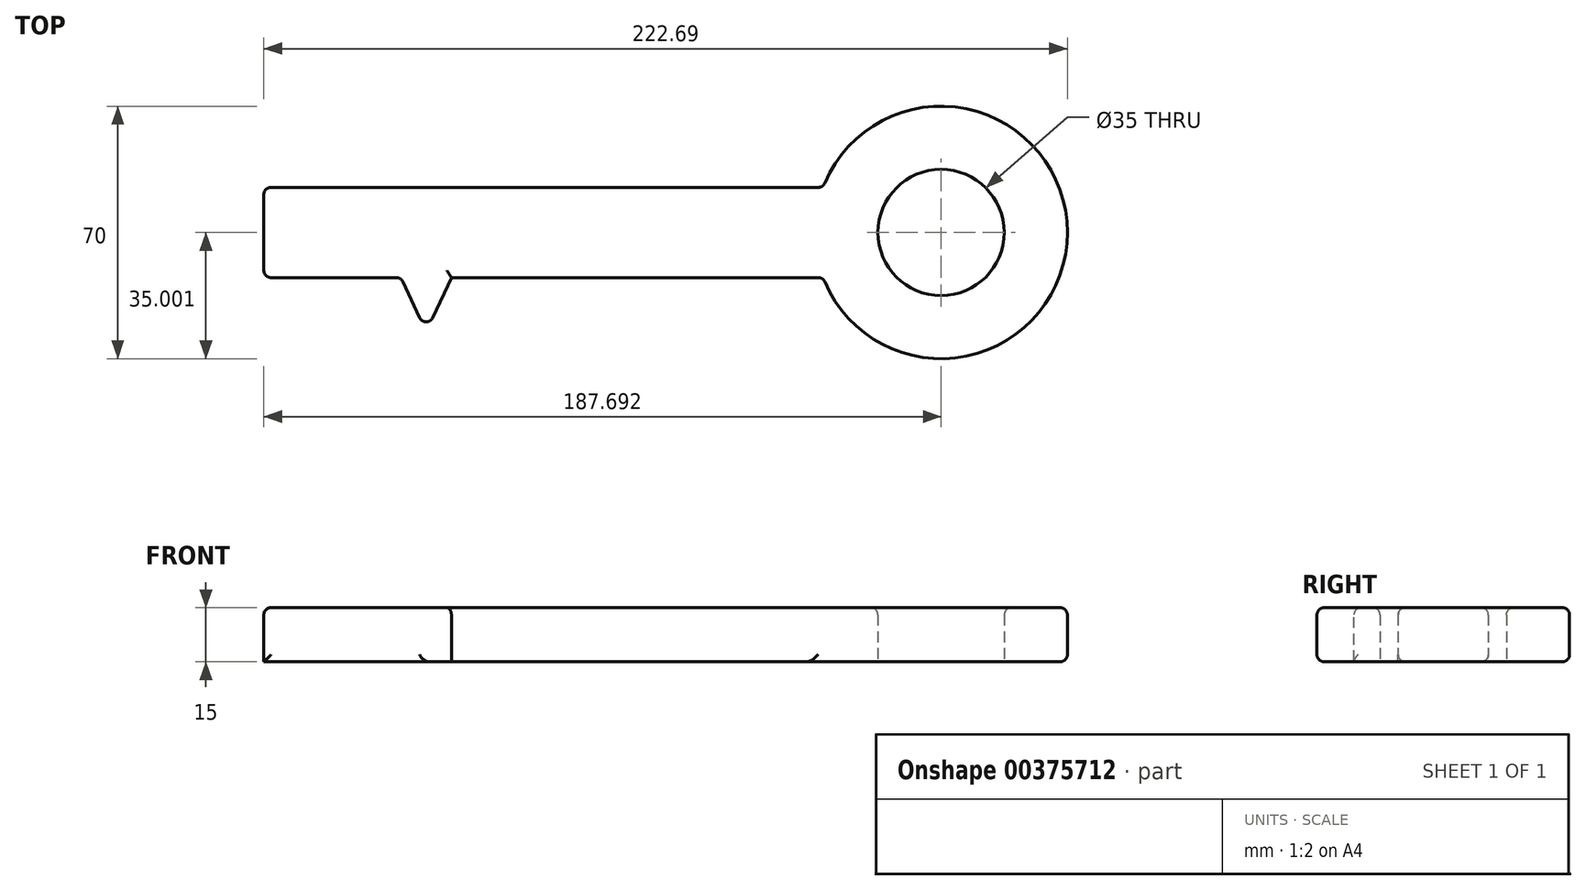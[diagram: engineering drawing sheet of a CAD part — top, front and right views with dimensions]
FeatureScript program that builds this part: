
annotation { "Feature Type Name" : "Feature", "Feature Type Description" : "" }
export const myFeature = defineFeature(function(context is Context, id is Id, definition is map)
    precondition{}
    {
        {
            var Q0;
            Q0=qCreatedBy(makeId("Top.planeOp"),FACE);
            var sketch = newSketch(context, id + "F0", { "sketchPlane" : qUnion([Q0])});
            skLineSegment(sketch, "E0.bottom", {"start": v(-155, 9.98) * mm, "end": v(0, 9.98) * mm});
            skLineSegment(sketch, "E0.top", {"start": v(-155, -15.02) * mm, "end": v(0, -15.02) * mm});
            skLineSegment(sketch, "E0.left", {"start": v(-155, 9.98) * mm, "end": v(-155, -15.02) * mm});
            skLineSegment(sketch, "E0.right", {"start": v(0, 9.98) * mm, "end": v(0, -15.02) * mm});
            skLineSegment(sketch, "E1.bottom", {"start": v(-155, -15.02) * mm, "end": v(-145, -15.02) * mm});
            skLineSegment(sketch, "E1.top", {"start": v(-155, -45.02) * mm, "end": v(-145, -45.02) * mm});
            skLineSegment(sketch, "E1.left", {"start": v(-155, -15.02) * mm, "end": v(-155, -45.02) * mm});
            skLineSegment(sketch, "E1.right", {"start": v(-145, -15.02) * mm, "end": v(-145, -45.02) * mm});
            skLineSegment(sketch, "E2.bottom", {"start": v(-135, -15.02) * mm, "end": v(-127, -15.02) * mm});
            skLineSegment(sketch, "E2.top", {"start": v(-135, -30.02) * mm, "end": v(-127, -30.02) * mm});
            skLineSegment(sketch, "E2.left", {"start": v(-135, -15.02) * mm, "end": v(-135, -30.02) * mm});
            skLineSegment(sketch, "E2.right", {"start": v(-127, -15.02) * mm, "end": v(-127, -30.02) * mm});
            skLineSegment(sketch, "E3", {"start": v(-117, -15.02) * mm, "end": v(-110, -30.02) * mm});
            skLineSegment(sketch, "E4", {"start": v(-103, -15.02) * mm, "end": v(-110, -30.02) * mm});
            skArc(sketch, "E5", {"start": v(0, -15.02) * mm, "mid": v(67.7, -2.52) * mm, "end": v(0, 9.98) * mm});
            skCircle(sketch, "E6", {"center": v(32.7, -2.52) * mm, "radius": 17.5 * mm});
            skSolve(sketch);
        }
        {
            var Q0;
            Q0=makeQuery(id+"F0.imprint","IMPRINT",FACE,{"disambiguationData":[TD([[makeQuery(id+"F0.imprint","IMPRINT",EDGE,{"derivedFrom":sQuery(id+"F0.wireOp",EDGE,"E0.bottom")}),-1.0]])]});
            var Q1;
            Q1=makeQuery(id+"F0.imprint","IMPRINT",FACE,{"disambiguationData":[TD([[makeQuery(id+"F0.imprint","IMPRINT",EDGE,{"derivedFrom":sQuery(id+"F0.wireOp",EDGE,"E1.bottom")}),-1.0]])]});
            var Q2;
            Q2=makeQuery(id+"F0.imprint","IMPRINT",FACE,{"disambiguationData":[TD([[makeQuery(id+"F0.imprint","IMPRINT",EDGE,{"derivedFrom":sQuery(id+"F0.wireOp",EDGE,"E2.bottom")}),-1.0]])]});
            var Q3;
            {var subQ0=sQuery(id+"F0.wireOp",EDGE,"E3");Q3=makeQuery(id+"F0.imprint","IMPRINT",FACE,{"disambiguationData":[TD([[makeQuery(id+"F0.imprint","IMPRINT",EDGE,{"derivedFrom":subQ0}),1.0]])]});}
            var Q4;
            Q4=makeQuery(id+"F0.imprint","IMPRINT",FACE,{"disambiguationData":[TD([[makeQuery(id+"F0.imprint","IMPRINT",EDGE,{"derivedFrom":sQuery(id+"F0.wireOp",EDGE,"E0.right")}),1.0]])]});
            extrude(context, id + "F1", {"entities" : qUnion([Q0, Q1, Q2, Q3, Q4]), "depth" : 15 * mm});
        }
        {
            var Q0;
            Q0=makeQuery(id+"F1.opExtrude","CAP_EDGE",EDGE,{"disambiguationData":[OSD([sQuery(id+"F0.wireOp",EDGE,"E0.bottom")])],"isStart":false});
            var Q1;
            Q1=makeQuery(id+"F1.opExtrude","CAP_EDGE",EDGE,{"disambiguationData":[OSD([sQuery(id+"F0.wireOp",EDGE,"E0.left"),sQuery(id+"F0.wireOp",EDGE,"E1.left")])],"isStart":false});
            var Q2;
            Q2=makeQuery(id+"F1.opExtrude","CAP_EDGE",EDGE,{"disambiguationData":[OSD([sQuery(id+"F0.wireOp",EDGE,"E1.right")])],"isStart":false});
            var Q3;
            {var subQ0=sQuery(id+"F0.wireOp",EDGE,"E0.top");Q3=makeQuery(id+"F1.opExtrude","CAP_EDGE",EDGE,{"disambiguationData":[OSD([subQ0]),TDD([makeQuery(id+"F0.imprint","IMPRINT",EDGE,{"disambiguationData":[TD([[makeQuery(id+"F0.imprint","INTERSECT",VERTEX,{"derivedFrom":[subQ0,sQuery(id+"F0.wireOp",EDGE,"E1.bottom"),sQuery(id+"F0.wireOp",EDGE,"E1.right")]}),-1.0]])],"derivedFrom":subQ0})])],"isStart":false});}
            var Q4;
            Q4=makeQuery(id+"F1.opExtrude","CAP_EDGE",EDGE,{"disambiguationData":[OSD([sQuery(id+"F0.wireOp",EDGE,"E2.left")])],"isStart":false});
            var Q5;
            Q5=makeQuery(id+"F1.opExtrude","CAP_EDGE",EDGE,{"disambiguationData":[OSD([sQuery(id+"F0.wireOp",EDGE,"E2.right")])],"isStart":false});
            var Q6;
            Q6=makeQuery(id+"F1.opExtrude","CAP_EDGE",EDGE,{"disambiguationData":[OSD([sQuery(id+"F0.wireOp",EDGE,"E2.top")])],"isStart":false});
            var Q7;
            Q7=makeQuery(id+"F1.opExtrude","CAP_EDGE",EDGE,{"disambiguationData":[OSD([sQuery(id+"F0.wireOp",EDGE,"E3")])],"isStart":false});
            var Q8;
            {var subQ0=sQuery(id+"F0.wireOp",EDGE,"E0.top");Q8=makeQuery(id+"F1.opExtrude","CAP_EDGE",EDGE,{"disambiguationData":[OSD([subQ0]),TDD([makeQuery(id+"F0.imprint","IMPRINT",EDGE,{"disambiguationData":[TD([[makeQuery(id+"F0.imprint","INTERSECT",VERTEX,{"derivedFrom":[subQ0,sQuery(id+"F0.wireOp",EDGE,"E4")]}),-1.0]])],"derivedFrom":subQ0})])],"isStart":false});}
            var Q9;
            Q9=makeQuery(id+"F1.opExtrude","CAP_EDGE",EDGE,{"disambiguationData":[OSD([sQuery(id+"F0.wireOp",EDGE,"E4")])],"isStart":false});
            var Q10;
            Q10=makeQuery(id+"F1.opExtrude","CAP_EDGE",EDGE,{"disambiguationData":[OSD([sQuery(id+"F0.wireOp",EDGE,"E5")])],"isStart":false});
            var Q11;
            Q11=makeQuery(id+"F1.opExtrude","CAP_EDGE",EDGE,{"disambiguationData":[OSD([sQuery(id+"F0.wireOp",EDGE,"E6")])],"isStart":false});
            var Q12;
            Q12=makeQuery(id+"F1.opExtrude","SWEPT_EDGE",EDGE,{"disambiguationData":[OSD([sQuery(id+"F0.wireOp",EDGE,"E0.top"),sQuery(id+"F0.wireOp",EDGE,"E3")])]});
            var Q13;
            Q13=makeQuery(id+"F1.opExtrude","SWEPT_FACE",FACE,{"disambiguationData":[OSD([sQuery(id+"F0.wireOp",EDGE,"E2.top")])]});
            var Q14;
            {var subQ0=sQuery(id+"F0.wireOp",EDGE,"E0.top");Q14=makeQuery(id+"F1.opExtrude","SWEPT_FACE",FACE,{"disambiguationData":[OSD([subQ0]),TDD([makeQuery(id+"F0.imprint","IMPRINT",EDGE,{"disambiguationData":[TD([[makeQuery(id+"F0.imprint","INTERSECT",VERTEX,{"derivedFrom":[subQ0,sQuery(id+"F0.wireOp",EDGE,"E1.bottom"),sQuery(id+"F0.wireOp",EDGE,"E1.right")]}),-1.0]])],"derivedFrom":subQ0})])]});}
            var Q15;
            Q15=makeQuery(id+"F1.opExtrude","SWEPT_FACE",FACE,{"disambiguationData":[OSD([sQuery(id+"F0.wireOp",EDGE,"E1.top")])]});
            var Q16;
            {var subQ0=sQuery(id+"F0.wireOp",EDGE,"E0.top");Q16=makeQuery(id+"F1.opExtrude","SWEPT_FACE",FACE,{"disambiguationData":[OSD([subQ0]),TDD([makeQuery(id+"F0.imprint","IMPRINT",EDGE,{"disambiguationData":[TD([[makeQuery(id+"F0.imprint","INTERSECT",VERTEX,{"derivedFrom":[subQ0,sQuery(id+"F0.wireOp",EDGE,"E3")]}),1.0]])],"derivedFrom":subQ0})])]});}
            var Q17;
            Q17=makeQuery(id+"F1.opExtrude","SWEPT_EDGE",EDGE,{"disambiguationData":[OSD([sQuery(id+"F0.wireOp",EDGE,"E2.top"),sQuery(id+"F0.wireOp",EDGE,"E2.left")])]});
            var Q18;
            Q18=makeQuery(id+"F1.opExtrude","SWEPT_EDGE",EDGE,{"disambiguationData":[OSD([sQuery(id+"F0.wireOp",EDGE,"E3"),sQuery(id+"F0.wireOp",EDGE,"E4")])]});
            var Q19;
            Q19=makeQuery(id+"F1.opExtrude","SWEPT_FACE",FACE,{"disambiguationData":[OSD([sQuery(id+"F0.wireOp",EDGE,"E3")])]});
            var Q20;
            Q20=makeQuery(id+"F1.opExtrude","SWEPT_FACE",FACE,{"disambiguationData":[OSD([sQuery(id+"F0.wireOp",EDGE,"E5")])]});
            var Q21;
            Q21=makeQuery(id+"F1.opExtrude","SWEPT_FACE",FACE,{"disambiguationData":[OSD([sQuery(id+"F0.wireOp",EDGE,"E0.bottom")])]});
            fillet(context, id + "F2", {"entities" : qUnion([Q0, Q1, Q2, Q3, Q4, Q5, Q6, Q7, Q8, Q9, Q10, Q11, Q12, Q13, Q14, Q15, Q16, Q17, Q18, Q19, Q20, Q21]), "radius" : 2 * mm, "tangentPropagation" : true, "allowEdgeOverflow" : false});
        }
    });
